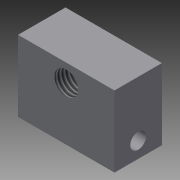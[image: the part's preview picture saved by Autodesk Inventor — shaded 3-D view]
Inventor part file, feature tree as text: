
AUTODESK INVENTOR PART (.ipt)
format: ipt  version: 2015 (Build 190159000, 159)  size: 96,256 bytes
history: native  units: in
note: dims shown in document units (in); Inventor stores cm internally (conversion verified against a paired STEP export)
features: extrude x3, sketch x3, thread x1
ambient origin geometry x8: Origin, YZ Plane, XZ Plane, XY Plane, X Axis, Y Axis, Z Axis, Center Point
bodies: Solid1 (feature_tree)
feature tree (7):
  extrude  "Extrusion1"  Depth=1.125in
  extrude  "Extrusion2"  Depth=0.75in
  extrude  "Extrusion3"  Depth=0.25in
  thread  "Thread1"  [1 undecoded]
  sketch  "Sketch1"  dims[d0=1.525in d1=1.125in]
  sketch  "Sketch2"  dims[d2=0.75in d3=0.0in d4=0.5in]
  sketch  "Sketch3"  dims[d5=0.25in d6=0.25in d7=3.0in d8=0.0in d9=0.375in d10=3.0in d11=0.0in d12=1.0in d13=0.0in]
note: 1 required parameter value undecoded (feature->parameter linkage not recoverable at this tier; creation-order binding heuristic only, values carry confidence <= 0.55)
